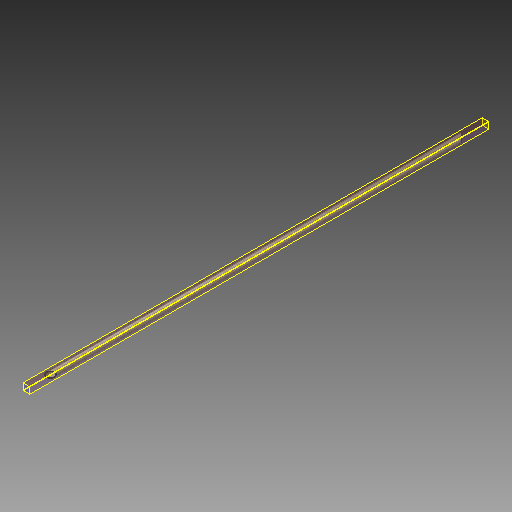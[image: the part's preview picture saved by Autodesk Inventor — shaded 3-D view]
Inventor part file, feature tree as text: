
AUTODESK INVENTOR PART (.ipt)
format: ipt  version: 2018 (Build 220112000, 112)  size: 95,744 bytes
history: native  units: mm
features: other x6, extrude x1, sketch x1
ambient origin geometry x8: Origin, YZ Plane, XZ Plane, XY Plane, X Axis, Y Axis, Z Axis, Center Point
bodies: Body1 (feature_tree)
feature tree (8):
  extrude  "押し出し2"  Depth=27.2mm
  other  "面の勾配1"
  other  "面の勾配2"
  other  "作業平面2"
  other  "作業平面4"
  other  "作業平面5"
  other  "作業平面6"
  sketch  "スケッチ3"
